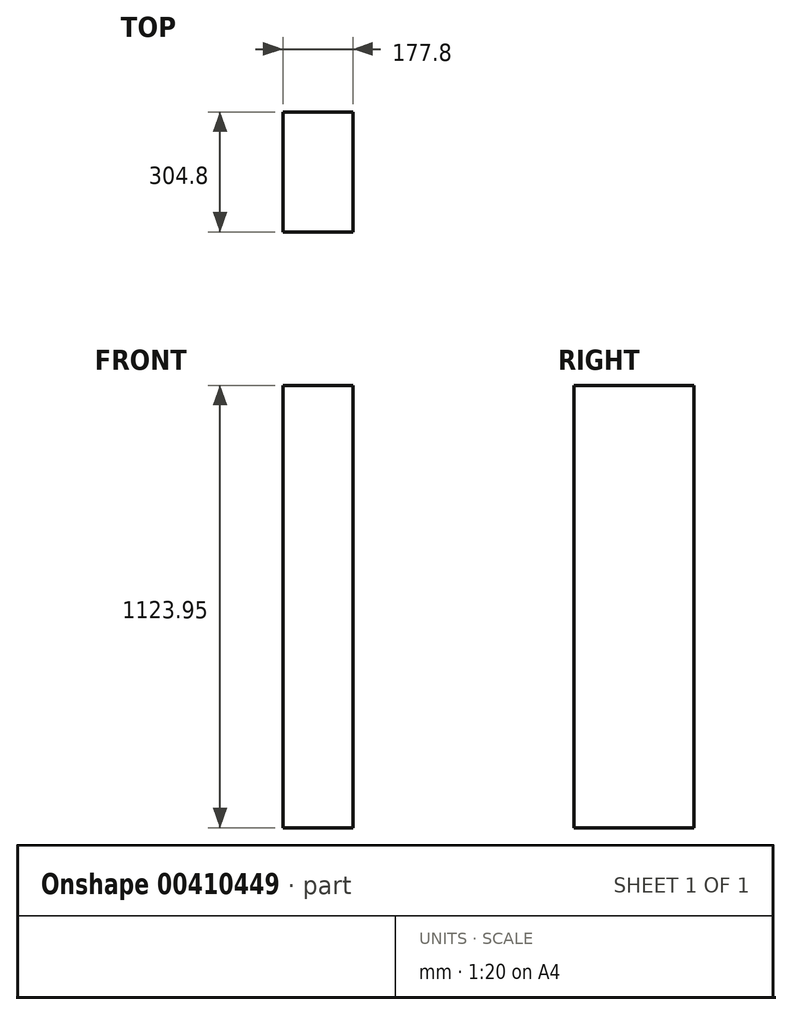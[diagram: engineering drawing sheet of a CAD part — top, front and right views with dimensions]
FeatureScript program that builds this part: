
annotation { "Feature Type Name" : "Feature", "Feature Type Description" : "" }
export const myFeature = defineFeature(function(context is Context, id is Id, definition is map)
    precondition{}
    {
        {
            var Q0;
            Q0=qCreatedBy(makeId("Right.planeOp"),FACE);
            var sketch = newSketch(context, id + "F0", { "sketchPlane" : qUnion([Q0])});
            skLineSegment(sketch, "E0.bottom", {"start": v(0, 0) * mm, "end": v(304.8, 0) * mm});
            skLineSegment(sketch, "E0.top", {"start": v(0, 1123.95) * mm, "end": v(304.8, 1123.95) * mm});
            skLineSegment(sketch, "E0.left", {"start": v(0, 0) * mm, "end": v(0, 1123.95) * mm});
            skLineSegment(sketch, "E0.right", {"start": v(304.8, 0) * mm, "end": v(304.8, 1123.95) * mm});
            skSolve(sketch);
        }
        {
            var Q0;
            Q0 = qSketchRegion(id + "F0", true);
            extrude(context, id + "F1", {"entities" : qUnion([Q0]), "depth" : 177.8 * mm, "offsetDistance" : 25.4 * mm});
        }
    });
